# Revit family: Tempest-Lantern_Lantern-Pole-Mount
name_source: partatom
category: Specialty Equipment
units: mm (PartAtom-declared; Revit-internal decimal feet)

## family parameters
Always vertical = Yes
Cut with Voids When Loaded = No
Enable Cutting in Views = No
Maintain Annotation Orientation = No
Part Type = Normal
Room Calculation Point = No
Round Connector Dimension = Use Radius
Shared = No
Work Plane-Based = No

## types (1)
- Tempest Lanterns Post
    CAD URL = https://www.arcat.com
    Cost = 0 $
    Default Elevation = 0' - 0"
    Glass = Glass
    Height = 6' - 2"
    Keynote = 26 56 00
    Lantern Body Height = 2' - 5 15/32"
    Lantern Body Width = 0' - 9 1/2"
    Load = 0 VA
    Manufacturer = Tempest Torch
    Metal = Body
    Model = Tempest Lanterns Post
    Pipe Connection Radius = 0' - 3"
    Pole = 1
    Post Dia = 0' - 3"
    Post Radius = 0' - 1 1/2"
    Product Documentation Link = https://www.travisindustries.com
    Product Page URL = https://www.tempesttorch.com
    Products URL = https://www.arcat.com
    Specification = https://www.tempesttorch.com
    Specifications URL = https://www.arcat.com
    URL = www.tempesttorch.com
    Voltage = 0 V

## geometry (parser evidence)
native form markers: Sweep x6
no freeform markers — native parametric forms only
